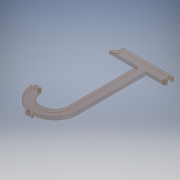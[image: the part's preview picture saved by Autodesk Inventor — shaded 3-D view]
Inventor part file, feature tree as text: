
AUTODESK INVENTOR PART (.ipt)
format: ipt  version: 2017 (Build 210142000, 142)  size: 152,064 bytes
history: native  units: mm
features: extrude x1, sketch x1
ambient origin geometry x8: Origin, YZ Plane, XZ Plane, XY Plane, X Axis, Y Axis, Z Axis, Center Point
bodies: Solid1 (feature_tree)
feature tree (2):
  extrude  "Extrusion1"  Depth=112.603506mm
  sketch  "Sketch1"  dims[d5=5.0mm d7=50.0mm d11=3.17mm d12=0.0mm d16=37.5mm d17=10.0mm d18=75.0mm d20=3.0mm d22=3.0mm d25=60.0deg d26=60.0deg d28=75.0mm d29=90.0deg d31=10.0mm d32=45.0deg d33=5.0mm d39=3.0mm d41=3.0mm d42=60.0deg d43=60.0deg d45=3.0mm d46=19.989518mm d47=24.990566mm d48=45.838996mm d49=3.0mm d50=4.0mm d51=60.0deg d52=4.0mm d53=25.0mm d54=25.0mm d55=15.0mm d56=44.986373mm d57=112.603506mm]
